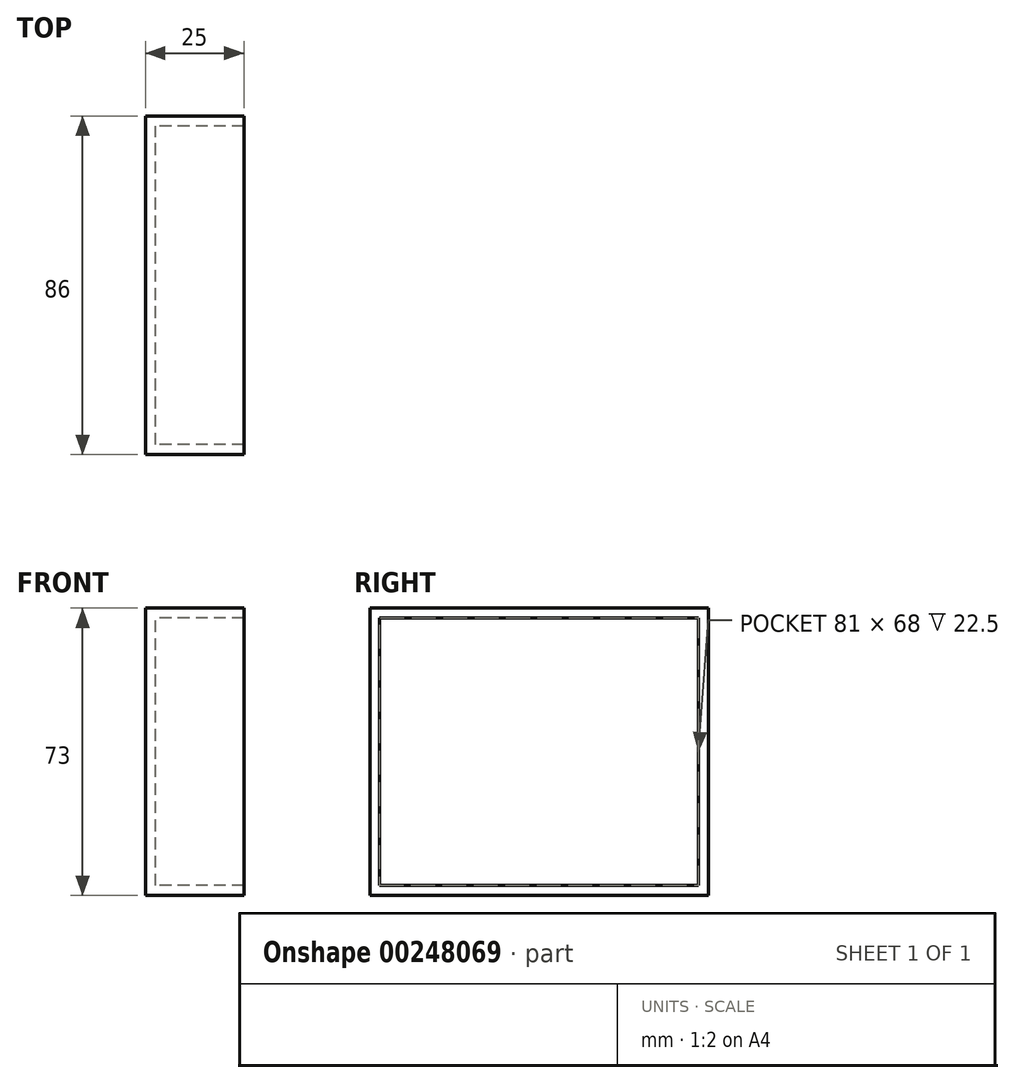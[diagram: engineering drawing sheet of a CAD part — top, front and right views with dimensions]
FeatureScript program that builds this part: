
annotation { "Feature Type Name" : "Feature", "Feature Type Description" : "" }
export const myFeature = defineFeature(function(context is Context, id is Id, definition is map)
    precondition{}
    {
        {
            var Q0;
            Q0=qCreatedBy(makeId("Right.planeOp"),FACE);
            var sketch = newSketch(context, id + "F0", { "sketchPlane" : qUnion([Q0])});
            skLineSegment(sketch, "E0.bottom", {"start": v(-43, -36.5) * mm, "end": v(43, -36.5) * mm});
            skLineSegment(sketch, "E0.top", {"start": v(-43, 36.5) * mm, "end": v(43, 36.5) * mm});
            skLineSegment(sketch, "E0.left", {"start": v(-43, -36.5) * mm, "end": v(-43, 36.5) * mm});
            skLineSegment(sketch, "E0.right", {"start": v(43, -36.5) * mm, "end": v(43, 36.5) * mm});
            skPoint(sketch, "E0.middle", {"position": v(0, 0) * mm});
            skSolve(sketch);
        }
        {
            var Q0;
            Q0=makeQuery(id+"F0.imprint","IMPRINT",FACE,{"disambiguationData":[TD([[makeQuery(id+"F0.imprint","IMPRINT",EDGE,{"derivedFrom":sQuery(id+"F0.wireOp",EDGE,"E0.bottom")}),1.0]])]});
            extrude(context, id + "F1", {"entities" : qUnion([Q0]), "depth" : 25 * mm});
        }
        {
            var Q0;
            Q0=makeQuery(id+"F1.opExtrude","CAP_FACE",FACE,{"disambiguationData":[OSD([sQuery(id+"F0.wireOp",EDGE,"E0.bottom"),sQuery(id+"F0.wireOp",EDGE,"E0.top"),sQuery(id+"F0.wireOp",EDGE,"E0.left"),sQuery(id+"F0.wireOp",EDGE,"E0.right")])],"isStart":false});
            shell(context, id + "F2", {"entities" : qUnion([Q0]), "thickness" : 2.5 * mm});
        }
    });
